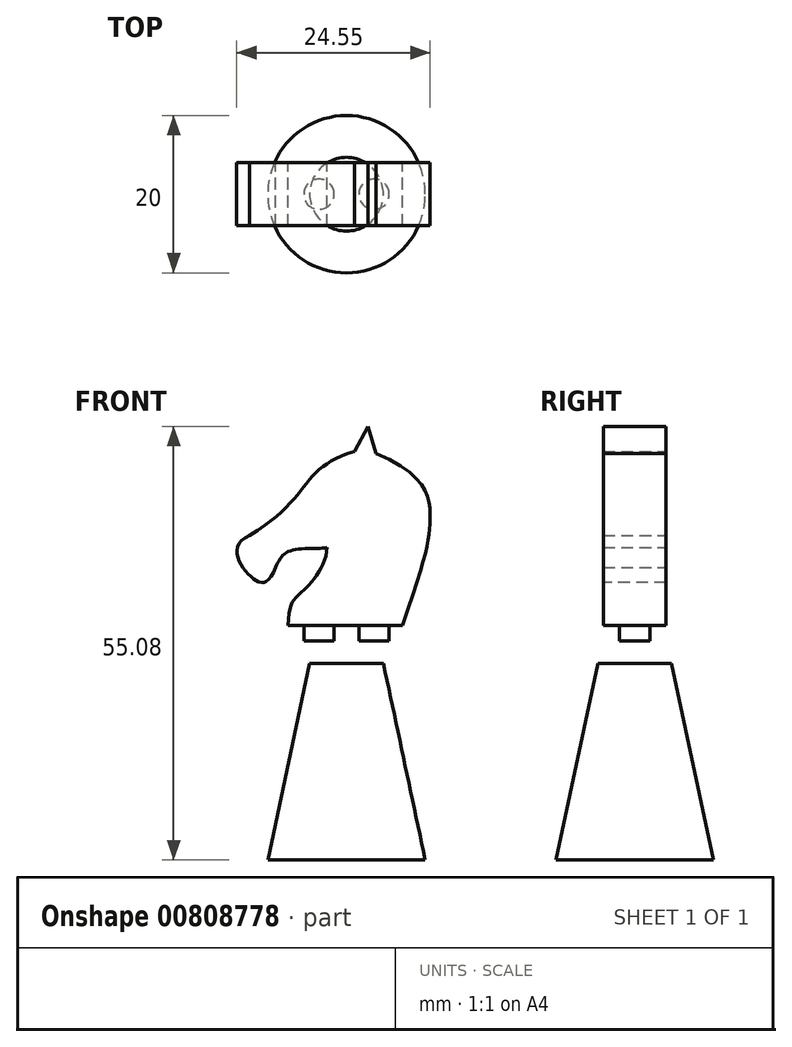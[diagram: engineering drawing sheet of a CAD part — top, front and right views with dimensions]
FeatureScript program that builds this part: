
annotation { "Feature Type Name" : "Feature", "Feature Type Description" : "" }
export const myFeature = defineFeature(function(context is Context, id is Id, definition is map)
    precondition{}
    {
        {
            var Q0;
            Q0=qCreatedBy(makeId("Top.planeOp"),FACE);
            var sketch = newSketch(context, id + "F0", { "sketchPlane" : qUnion([Q0])});
            skCircle(sketch, "E0", {"center": v(0, 0) * mm, "radius": 12.5 * mm});
            skSolve(sketch);
        }
        {
            var Q0;
            Q0=qCreatedBy(makeId("Top.planeOp"),FACE);
            cPlane(context, id + "F1", {"entities" : qUnion([Q0]), "cplaneType" : CPlaneType.OFFSET, "offset" : 10 * mm, "oppositeDirection" : true, "width" : 150 * mm, "height" : 150 * mm});
        }
        {
            var Q0;
            Q0=qCreatedBy(id+"F1.planeOp",FACE);
            var sketch = newSketch(context, id + "F2", { "sketchPlane" : qUnion([Q0])});
            skCircle(sketch, "E1", {"center": v(0, 0) * mm, "radius": 16 * mm});
            skSolve(sketch);
        }
        {
            var Q0;
            Q0=qCreatedBy(makeId("Top.planeOp"),FACE);
            var sketch = newSketch(context, id + "F3", { "sketchPlane" : qUnion([Q0])});
            skCircle(sketch, "E2", {"center": v(0, 0) * mm, "radius": 10 * mm});
            skSolve(sketch);
        }
        {
            var Q0;
            Q0=makeQuery(id+"F3.imprint","IMPRINT",FACE,{"disambiguationData":[TD([[makeQuery(id+"F3.imprint","IMPRINT",EDGE,{"derivedFrom":sQuery(id+"F3.wireOp",EDGE,"E2")}),1.0]])]});
            extrude(context, id + "F4", {"entities" : qUnion([Q0]), "depth" : 25 * mm, "hasDraft" : true, "draftAngle" : 12 * degree, "draftPullDirection" : true});
        }
        {
            var Q0;
            Q0=qCreatedBy(makeId("Front.planeOp"),FACE);
            var sketch = newSketch(context, id + "F5", { "sketchPlane" : qUnion([Q0])});
            skLineSegment(sketch, "E3", {"start": v(1, 51.9) * mm, "end": v(2.75, 55.08) * mm});
            skLineSegment(sketch, "E4", {"start": v(2.75, 55.08) * mm, "end": v(3.75, 51.64) * mm});
            skLineSegment(sketch, "E5", {"start": v(7.1, 29.82) * mm, "end": v(-7.42, 29.82) * mm});
            skFitSpline(sketch, "E6", {"points": [v(-9.02, 37.15) * mm, v(-12.24, 36.11) * mm, v(-12.3, 41.24) * mm], "startDerivative": vector(-6.43, -16.65) * mm, "endDerivative": vector(15.61, 6.41) * mm});
            skFitSpline(sketch, "E7", {"points": [v(3.75, 51.64) * mm, v(10.61, 43.56) * mm, v(7.1, 29.82) * mm], "startDerivative": vector(43.12, -18.02) * mm, "endDerivative": vector(-17.86, -51.15) * mm});
            skFitSpline(sketch, "E8", {"points": [v(-12.3, 41.24) * mm, v(1, 51.9) * mm], "startDerivative": vector(24.1, 14.49) * mm, "endDerivative": vector(20.98, 5.99) * mm});
            skFitSpline(sketch, "E9", {"points": [v(-7.42, 29.82) * mm, v(-5.47, 34.22) * mm, v(-2.48, 39.7) * mm], "startDerivative": vector(0.56, 20.85) * mm, "endDerivative": vector(0.47, 12.19) * mm});
            skFitSpline(sketch, "E10", {"points": [v(-9.02, 37.15) * mm, v(-7.07, 39.3) * mm, v(-2.48, 39.7) * mm], "startDerivative": vector(3.09, 7.13) * mm, "endDerivative": vector(5.27, 1.22) * mm});
            skSolve(sketch);
        }
        {
            var Q0;
            Q0=makeQuery(id+"F5.imprint","IMPRINT",FACE,{"disambiguationData":[TD([[makeQuery(id+"F5.imprint","IMPRINT",EDGE,{"derivedFrom":sQuery(id+"F5.wireOp",EDGE,"E3")}),-1.0]])]});
            extrude(context, id + "F6", {"entities" : qUnion([Q0]), "endBound" : BoundingType.SYMMETRIC, "depth" : 8 * mm, "offsetDistance" : 25 * mm});
        }
        {
            var Q0;
            Q0=makeQuery(id+"F6.opExtrude","SWEPT_FACE",FACE,{"disambiguationData":[OSD([sQuery(id+"F5.wireOp",EDGE,"E5")])]});
            var sketch = newSketch(context, id + "F7", { "sketchPlane" : qUnion([Q0])});
            skCircle(sketch, "E11", {"center": v(-3.5, 0) * mm, "radius": 1.93 * mm});
            skCircle(sketch, "E12", {"center": v(3.5, 0) * mm, "radius": 1.93 * mm});
            skSolve(sketch);
        }
        {
            var Q0;
            Q0=makeQuery(id+"F7.imprint","IMPRINT",FACE,{"disambiguationData":[TD([[makeQuery(id+"F7.imprint","IMPRINT",EDGE,{"derivedFrom":sQuery(id+"F7.wireOp",EDGE,"E11")}),1.0]])]});
            var Q1;
            Q1=makeQuery(id+"F7.imprint","IMPRINT",FACE,{"disambiguationData":[TD([[makeQuery(id+"F7.imprint","IMPRINT",EDGE,{"derivedFrom":sQuery(id+"F7.wireOp",EDGE,"E12")}),1.0]])]});
            extrude(context, id + "F8", {"entities" : qUnion([Q0, Q1]), "operationType" : NewBodyOperationType.ADD, "depth" : 2 * mm, "offsetDistance" : 25 * mm});
        }
    });
